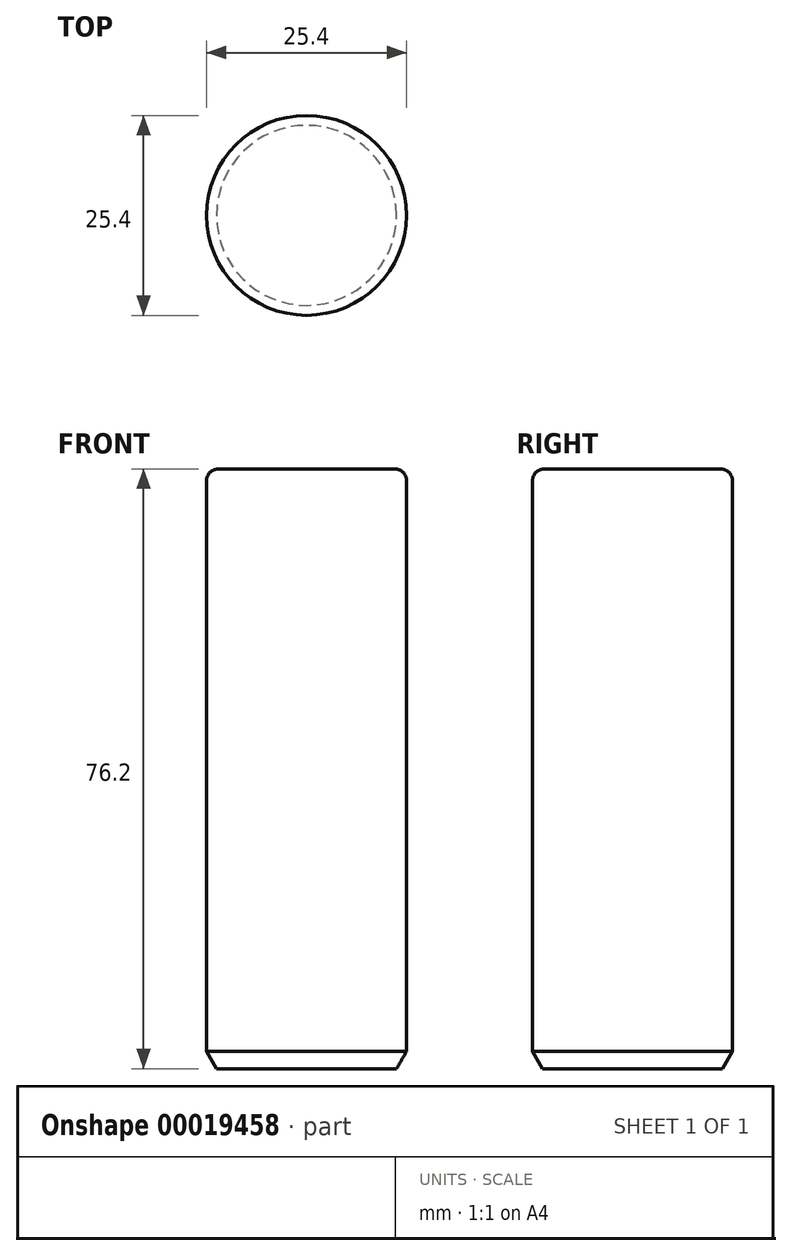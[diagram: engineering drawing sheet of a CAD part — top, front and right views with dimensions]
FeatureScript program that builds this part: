
annotation { "Feature Type Name" : "Feature", "Feature Type Description" : "" }
export const myFeature = defineFeature(function(context is Context, id is Id, definition is map)
    precondition{}
    {
        {
            var Q0;
            Q0=qCreatedBy(makeId("Top.planeOp"),FACE);
            var sketch = newSketch(context, id + "F0", { "sketchPlane" : qUnion([Q0])});
            skCircle(sketch, "E0", {"center": v(0, 0) * mm, "radius": 12.7 * mm});
            skSolve(sketch);
        }
        {
            var Q0;
            Q0 = qSketchRegion(id + "F0", true);
            extrude(context, id + "F1", {"entities" : qUnion([Q0]), "endBound" : BoundingType.SYMMETRIC, "depth" : 76.2 * mm});
        }
        {
            var Q0;
            Q0=makeQuery(id+"F1.opExtrude","CAP_EDGE",EDGE,{"disambiguationData":[OSD([sQuery(id+"F0.wireOp",EDGE,"E0")])],"isStart":false});
            fillet(context, id + "F2", {"entities" : qUnion([Q0]), "radius" : 1.52 * mm, "tangentPropagation" : true, "allowEdgeOverflow" : false});
        }
        {
            var Q0;
            Q0=makeQuery(id+"F1.opExtrude","CAP_EDGE",EDGE,{"disambiguationData":[OSD([sQuery(id+"F0.wireOp",EDGE,"E0")])],"isStart":true});
            chamfer(context, id + "F3", {"entities" : qUnion([Q0]), "chamferType" : ChamferType.OFFSET_ANGLE, "width" : 1.27 * mm, "oppositeDirection" : true, "angle" : 60 * degree, "tangentPropagation" : true});
        }
    });
